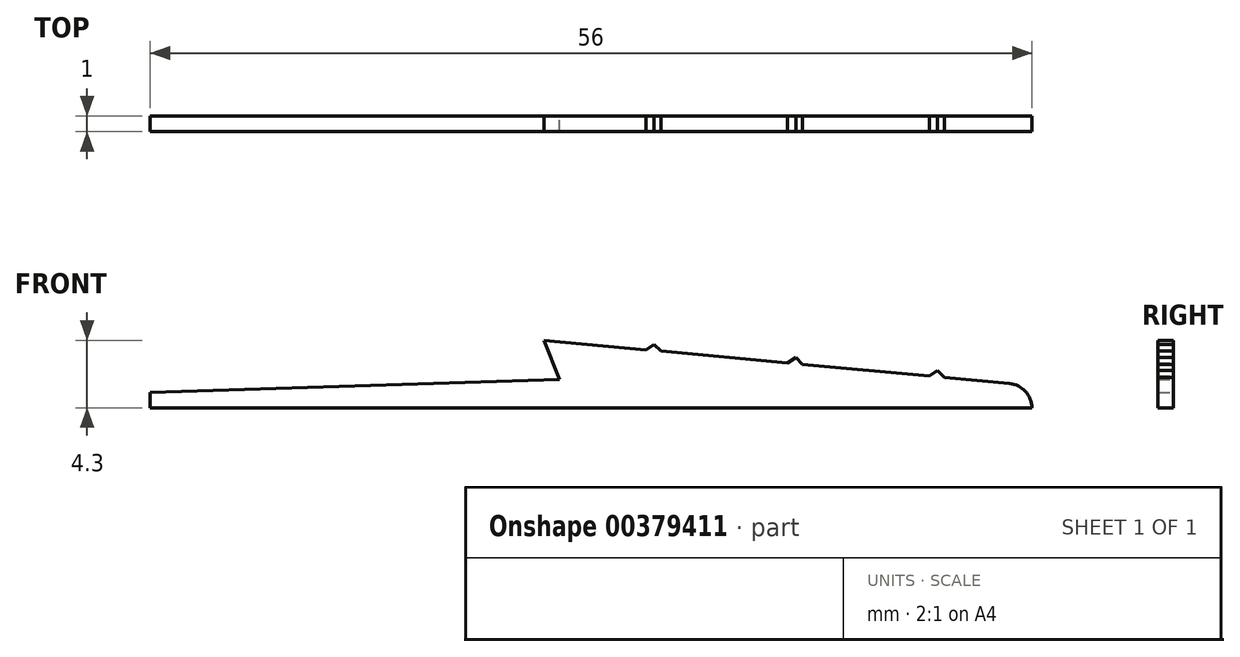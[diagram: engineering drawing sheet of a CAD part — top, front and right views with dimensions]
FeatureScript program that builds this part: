
annotation { "Feature Type Name" : "Feature", "Feature Type Description" : "" }
export const myFeature = defineFeature(function(context is Context, id is Id, definition is map)
    precondition{}
    {
        {
            var Q0;
            Q0=qCreatedBy(makeId("Front.planeOp"),FACE);
            var sketch = newSketch(context, id + "F0", { "sketchPlane" : qUnion([Q0])});
            skLineSegment(sketch, "E0", {"start": v(-55.35, -5.23) * mm, "end": v(0.65, -5.23) * mm});
            skLineSegment(sketch, "E1", {"start": v(-0.77, -3.68) * mm, "end": v(-4.91, -3.3) * mm});
            skLineSegment(sketch, "E2", {"start": v(-30.35, -0.93) * mm, "end": v(-29.35, -3.43) * mm});
            skLineSegment(sketch, "E3", {"start": v(-55.35, -5.23) * mm, "end": v(-55.35, -4.23) * mm});
            skLineSegment(sketch, "E4", {"start": v(-55.35, -4.23) * mm, "end": v(-29.35, -3.43) * mm});
            skArc(sketch, "E5", {"start": v(0.65, -5.23) * mm, "mid": v(0.24, -4.18) * mm, "end": v(-0.77, -3.68) * mm});
            skLineSegment(sketch, "E6", {"start": v(-23.35, -1.18) * mm, "end": v(-23.86, -1.54) * mm});
            skLineSegment(sketch, "E7", {"start": v(-23.35, -1.18) * mm, "end": v(-22.91, -1.62) * mm});
            skLineSegment(sketch, "E8", {"start": v(-14.35, -2.02) * mm, "end": v(-14.86, -2.37) * mm});
            skLineSegment(sketch, "E9", {"start": v(-14.35, -2.02) * mm, "end": v(-13.91, -2.46) * mm});
            skLineSegment(sketch, "E10", {"start": v(-5.35, -2.85) * mm, "end": v(-5.86, -3.2) * mm});
            skLineSegment(sketch, "E11", {"start": v(-5.35, -2.85) * mm, "end": v(-4.91, -3.3) * mm});
            skLineSegment(sketch, "E12.trimOffspring", {"start": v(-23.86, -1.54) * mm, "end": v(-30.35, -0.93) * mm});
            skLineSegment(sketch, "E13.trimOffspring", {"start": v(-14.86, -2.37) * mm, "end": v(-22.91, -1.62) * mm});
            skLineSegment(sketch, "E14.trimOffspring", {"start": v(-5.86, -3.2) * mm, "end": v(-13.91, -2.46) * mm});
            skSolve(sketch);
        }
        {
            var Q0;
            Q0 = qSketchRegion(id + "F0", true);
            extrude(context, id + "F1", {"entities" : qUnion([Q0]), "depth" : 1 * mm});
        }
    });
